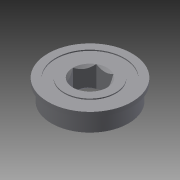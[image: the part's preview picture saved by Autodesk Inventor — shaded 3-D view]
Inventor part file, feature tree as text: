
AUTODESK INVENTOR PART (.ipt)
format: ipt  version: 2013 (Build 170138000, 138)  size: 162,304 bytes
history: native  units: in
note: dims shown in document units (in); Inventor stores cm internally (conversion verified against a paired STEP export)
features: sketch x4, extrude x2, hole x2, other x1, chamfer x1, imported_body x1
ambient origin geometry x8: Origin, YZ Plane, XZ Plane, XY Plane, X Axis, Y Axis, Z Axis, Center Point
feature tree (11):
  other  "Cut-Extrude1"
  extrude  "Extrusion1"  Depth=0.015in TaperAngle=0.0deg
  chamfer  "Chamfer1"  Distance=0.015in Angle=45.0deg
  extrude  "Extrusion2"  TaperAngle=0.0deg  [1 undecoded]
  hole  "Hole3"  [1 undecoded]
  hole  "Hole4"  [1 undecoded]
  imported_body  "Base1"
  sketch  "Sketch3"  dims[d14=0.75in d15=0.015in d16=0.0in d17=0.015in d18=0.125in d19=45.0deg]
  sketch  "Sketch4"  dims[d20=0.25in d21=0.0in]
  sketch  "Sketch5"  dims[d22=0.3125in d23=0.0in]
  sketch  "Sketch6"  dims[d24=0.25in d25=0.75in d26=0.5in d27=0.25in d28=0.5772in d29=1.0in d30=0.8108in d31=0.25in d32=0.75in d33=0.5in d34=0.25in d35=0.5772in d36=1.0in d37=0.8108in]
note: 3 required parameter values undecoded (feature->parameter linkage not recoverable at this tier; creation-order binding heuristic only, values carry confidence <= 0.55)
